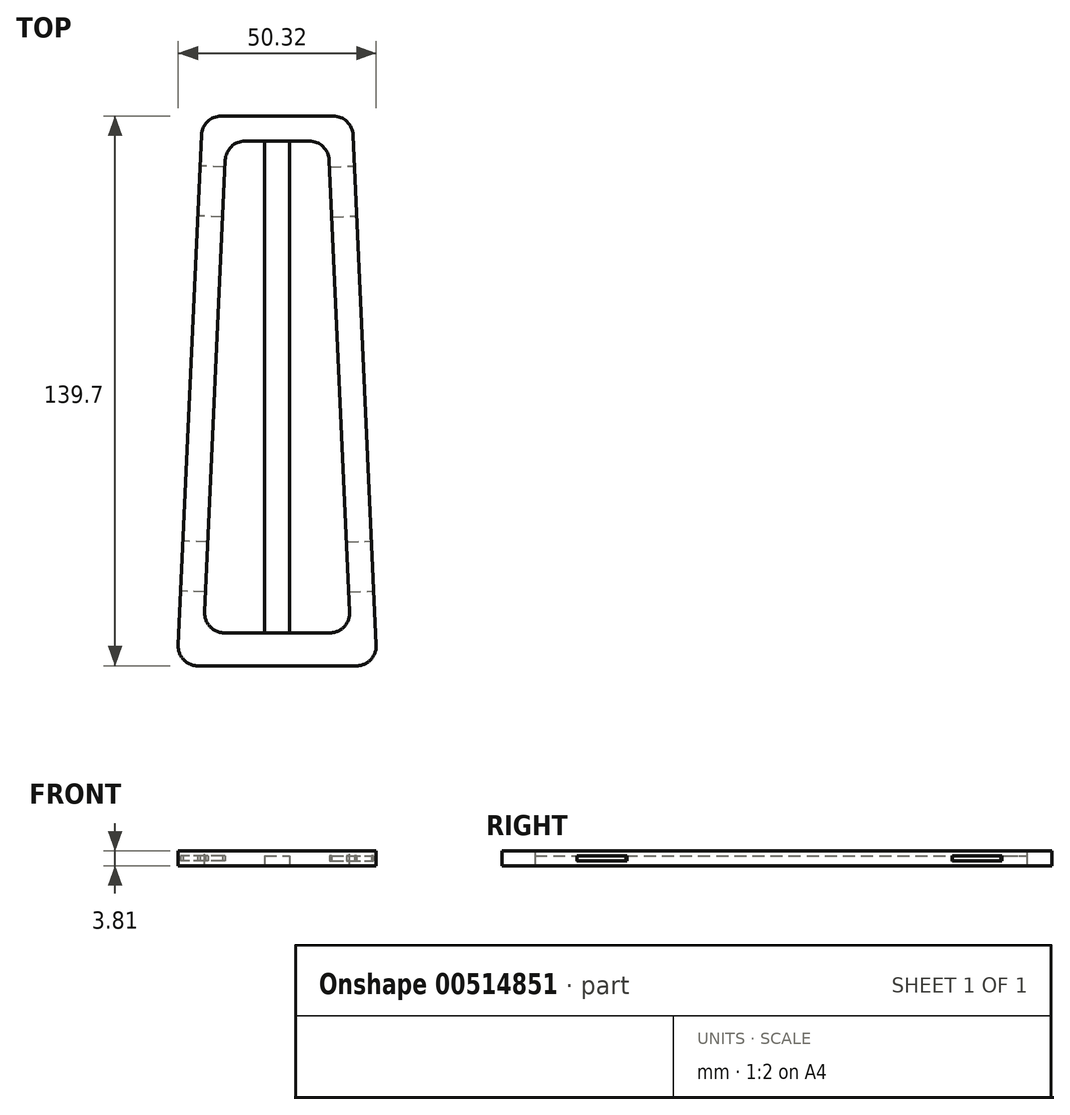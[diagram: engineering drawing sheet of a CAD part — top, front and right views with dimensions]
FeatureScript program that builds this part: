
annotation { "Feature Type Name" : "Feature", "Feature Type Description" : "" }
export const myFeature = defineFeature(function(context is Context, id is Id, definition is map)
    precondition{}
    {
        {
            var Q0;
            Q0=qCreatedBy(makeId("Top.planeOp"),FACE);
            var sketch = newSketch(context, id + "F0", { "sketchPlane" : qUnion([Q0])});
            skLineSegment(sketch, "E0", {"start": v(0, 0) * mm, "end": v(50.8, 0) * mm});
            skLineSegment(sketch, "E1", {"start": v(50.8, 0) * mm, "end": v(44.45, 139.7) * mm});
            skLineSegment(sketch, "E2", {"start": v(44.45, 139.7) * mm, "end": v(6.35, 139.7) * mm});
            skLineSegment(sketch, "E3", {"start": v(6.35, 139.7) * mm, "end": v(0, 0) * mm});
            skLineSegment(sketch, "E4", {"start": v(25.4, 0) * mm, "end": v(25.4, 139.7) * mm, "construction": true});
            skLineSegment(sketch, "E5", {"start": v(6.74, 8.38) * mm, "end": v(44.06, 8.38) * mm, "construction": true});
            skLineSegment(sketch, "E6", {"start": v(44.06, 8.38) * mm, "end": v(38.38, 133.35) * mm});
            skLineSegment(sketch, "E7", {"start": v(38.38, 133.35) * mm, "end": v(12.42, 133.35) * mm, "construction": true});
            skLineSegment(sketch, "E8", {"start": v(12.42, 133.35) * mm, "end": v(6.74, 8.38) * mm});
            skLineSegment(sketch, "E9", {"start": v(22.22, 8.38) * mm, "end": v(22.22, 133.35) * mm});
            skLineSegment(sketch, "E10", {"start": v(28.57, 8.38) * mm, "end": v(28.57, 133.35) * mm});
            skLineSegment(sketch, "E11", {"start": v(6.74, 8.38) * mm, "end": v(22.22, 8.38) * mm});
            skLineSegment(sketch, "E12", {"start": v(28.57, 8.38) * mm, "end": v(44.06, 8.38) * mm});
            skLineSegment(sketch, "E13", {"start": v(28.57, 133.35) * mm, "end": v(38.38, 133.35) * mm});
            skLineSegment(sketch, "E14", {"start": v(22.22, 133.35) * mm, "end": v(12.42, 133.35) * mm});
            skLineSegment(sketch, "E15", {"start": v(22.22, 8.38) * mm, "end": v(28.57, 8.38) * mm});
            skLineSegment(sketch, "E16", {"start": v(22.22, 133.35) * mm, "end": v(28.57, 133.35) * mm});
            skSolve(sketch);
        }
        {
            var Q0;
            Q0=makeQuery(id+"F0.imprint","IMPRINT",FACE,{"disambiguationData":[TD([[makeQuery(id+"F0.imprint","IMPRINT",EDGE,{"derivedFrom":sQuery(id+"F0.wireOp",EDGE,"E0")}),1.0]])]});
            extrude(context, id + "F1", {"entities" : qUnion([Q0]), "depth" : 3.8 * mm, "offsetDistance" : 25.4 * mm});
        }
        {
            var Q0;
            Q0=makeQuery(id+"F0.imprint","IMPRINT",FACE,{"disambiguationData":[TD([[makeQuery(id+"F0.imprint","IMPRINT",EDGE,{"derivedFrom":sQuery(id+"F0.wireOp",EDGE,"E9")}),-1.0]])]});
            extrude(context, id + "F2", {"entities" : qUnion([Q0]), "operationType" : NewBodyOperationType.ADD, "depth" : 2.54 * mm, "offsetDistance" : 25.4 * mm});
        }
        {
            var Q0;
            Q0=makeQuery(id+"F1.opExtrude","SWEPT_FACE",FACE,{"disambiguationData":[OSD([sQuery(id+"F0.wireOp",EDGE,"E3")])]});
            var sketch = newSketch(context, id + "F3", { "sketchPlane" : qUnion([Q0])});
            skLineSegment(sketch, "E17.bottom", {"start": v(-31.75, 2.54) * mm, "end": v(-19.05, 2.54) * mm});
            skLineSegment(sketch, "E17.top", {"start": v(-31.75, 1.27) * mm, "end": v(-19.05, 1.27) * mm});
            skLineSegment(sketch, "E17.left", {"start": v(-31.75, 2.54) * mm, "end": v(-31.75, 1.27) * mm});
            skLineSegment(sketch, "E17.right", {"start": v(-19.05, 2.54) * mm, "end": v(-19.05, 1.27) * mm});
            skPoint(sketch, "E18.firstSnap0", {"position": v(-25.4, 2.54) * mm});
            skPoint(sketch, "E18.oppositeSnap0", {"position": v(-25.4, 1.27) * mm});
            skLineSegment(sketch, "E18.bottom", {"start": v(-127.14, 2.54) * mm, "end": v(-114.44, 2.54) * mm});
            skLineSegment(sketch, "E18.top", {"start": v(-127.14, 1.27) * mm, "end": v(-114.44, 1.27) * mm});
            skLineSegment(sketch, "E18.left", {"start": v(-127.14, 2.54) * mm, "end": v(-127.14, 1.27) * mm});
            skLineSegment(sketch, "E18.right", {"start": v(-114.44, 2.54) * mm, "end": v(-114.44, 1.27) * mm});
            skLineSegment(sketch, "E19", {"start": v(-127.14, 2.54) * mm, "end": v(-127.14, 3.81) * mm, "construction": true});
            skLineSegment(sketch, "E20", {"start": v(-31.75, 2.54) * mm, "end": v(-31.75, 3.81) * mm, "construction": true});
            skLineSegment(sketch, "E21", {"start": v(-31.75, 1.27) * mm, "end": v(-31.75, 0) * mm, "construction": true});
            skLineSegment(sketch, "E22", {"start": v(-127.14, 1.27) * mm, "end": v(-127.14, 0) * mm, "construction": true});
            skSolve(sketch);
        }
        {
            var Q0;
            Q0=makeQuery(id+"F3.imprint","IMPRINT",FACE,{"disambiguationData":[TD([[makeQuery(id+"F3.imprint","IMPRINT",EDGE,{"derivedFrom":sQuery(id+"F3.wireOp",EDGE,"E18.bottom")}),-1.0]])]});
            var Q1;
            Q1=makeQuery(id+"F3.imprint","IMPRINT",FACE,{"disambiguationData":[TD([[makeQuery(id+"F3.imprint","IMPRINT",EDGE,{"derivedFrom":sQuery(id+"F3.wireOp",EDGE,"E17.bottom")}),-1.0]])]});
            extrude(context, id + "F4", {"entities" : qUnion([Q0, Q1]), "operationType" : NewBodyOperationType.REMOVE, "oppositeDirection" : true, "depth" : 6.35 * mm, "offsetDistance" : 25.4 * mm});
        }
        {
            var Q0;
            Q0=makeQuery(id+"F1.opExtrude","SWEPT_FACE",FACE,{"disambiguationData":[OSD([sQuery(id+"F0.wireOp",EDGE,"E1")])]});
            var sketch = newSketch(context, id + "F5", { "sketchPlane" : qUnion([Q0])});
            skLineSegment(sketch, "E23.bottom", {"start": v(16.74, 2.54) * mm, "end": v(29.44, 2.54) * mm});
            skLineSegment(sketch, "E23.top", {"start": v(16.74, 1.27) * mm, "end": v(29.44, 1.27) * mm});
            skLineSegment(sketch, "E23.left", {"start": v(16.74, 2.54) * mm, "end": v(16.74, 1.27) * mm});
            skLineSegment(sketch, "E23.right", {"start": v(29.44, 2.54) * mm, "end": v(29.44, 1.27) * mm});
            skLineSegment(sketch, "E24.bottom", {"start": v(112.14, 2.54) * mm, "end": v(124.84, 2.54) * mm});
            skLineSegment(sketch, "E24.top", {"start": v(112.14, 1.27) * mm, "end": v(124.84, 1.27) * mm});
            skLineSegment(sketch, "E24.left", {"start": v(112.14, 2.54) * mm, "end": v(112.14, 1.27) * mm});
            skLineSegment(sketch, "E24.right", {"start": v(124.84, 2.54) * mm, "end": v(124.84, 1.27) * mm});
            skLineSegment(sketch, "E25", {"start": v(124.84, 1.27) * mm, "end": v(124.84, 0) * mm, "construction": true});
            skLineSegment(sketch, "E26", {"start": v(124.84, 2.54) * mm, "end": v(124.84, 3.81) * mm, "construction": true});
            skLineSegment(sketch, "E27", {"start": v(29.44, 1.27) * mm, "end": v(29.44, 0) * mm, "construction": true});
            skLineSegment(sketch, "E28", {"start": v(29.44, 2.54) * mm, "end": v(29.44, 3.81) * mm, "construction": true});
            skSolve(sketch);
        }
        {
            var Q0;
            Q0 = qSketchRegion(id + "F5", true);
            extrude(context, id + "F6", {"entities" : qUnion([Q0]), "operationType" : NewBodyOperationType.REMOVE, "oppositeDirection" : true, "depth" : 6.35 * mm, "offsetDistance" : 25.4 * mm});
        }
        {
            var Q0;
            Q0=makeQuery(id+"F1.opExtrude","SWEPT_EDGE",EDGE,{"disambiguationData":[OSD([sQuery(id+"F0.wireOp",EDGE,"E0"),sQuery(id+"F0.wireOp",EDGE,"E3")])]});
            var Q1;
            Q1=makeQuery(id+"F1.opExtrude","SWEPT_EDGE",EDGE,{"disambiguationData":[OSD([sQuery(id+"F0.wireOp",EDGE,"E0"),sQuery(id+"F0.wireOp",EDGE,"E1")])]});
            var Q2;
            Q2=makeQuery(id+"F1.opExtrude","SWEPT_EDGE",EDGE,{"disambiguationData":[OSD([sQuery(id+"F0.wireOp",EDGE,"E8"),sQuery(id+"F0.wireOp",EDGE,"E11")])]});
            var Q3;
            Q3=makeQuery(id+"F2.opExtrude","SWEPT_EDGE",EDGE,{"disambiguationData":[OSD([sQuery(id+"F0.wireOp",EDGE,"E9"),sQuery(id+"F0.wireOp",EDGE,"E11"),sQuery(id+"F0.wireOp",EDGE,"E15")])]});
            var Q4;
            Q4=makeQuery(id+"F2.opExtrude","SWEPT_EDGE",EDGE,{"disambiguationData":[OSD([sQuery(id+"F0.wireOp",EDGE,"E10"),sQuery(id+"F0.wireOp",EDGE,"E12"),sQuery(id+"F0.wireOp",EDGE,"E15")])]});
            var Q5;
            Q5=makeQuery(id+"F1.opExtrude","SWEPT_EDGE",EDGE,{"disambiguationData":[OSD([sQuery(id+"F0.wireOp",EDGE,"E6"),sQuery(id+"F0.wireOp",EDGE,"E12")])]});
            var Q6;
            Q6=makeQuery(id+"F1.opExtrude","SWEPT_EDGE",EDGE,{"disambiguationData":[OSD([sQuery(id+"F0.wireOp",EDGE,"E8"),sQuery(id+"F0.wireOp",EDGE,"E14")])]});
            var Q7;
            Q7=makeQuery(id+"F2.opExtrude","SWEPT_EDGE",EDGE,{"disambiguationData":[OSD([sQuery(id+"F0.wireOp",EDGE,"E10"),sQuery(id+"F0.wireOp",EDGE,"E13"),sQuery(id+"F0.wireOp",EDGE,"E16")])]});
            var Q8;
            Q8=makeQuery(id+"F2.opExtrude","SWEPT_EDGE",EDGE,{"disambiguationData":[OSD([sQuery(id+"F0.wireOp",EDGE,"E9"),sQuery(id+"F0.wireOp",EDGE,"E14"),sQuery(id+"F0.wireOp",EDGE,"E16")])]});
            var Q9;
            Q9=makeQuery(id+"F1.opExtrude","SWEPT_EDGE",EDGE,{"disambiguationData":[OSD([sQuery(id+"F0.wireOp",EDGE,"E6"),sQuery(id+"F0.wireOp",EDGE,"E13")])]});
            var Q10;
            Q10=makeQuery(id+"F1.opExtrude","SWEPT_EDGE",EDGE,{"disambiguationData":[OSD([sQuery(id+"F0.wireOp",EDGE,"E2"),sQuery(id+"F0.wireOp",EDGE,"E3")])]});
            var Q11;
            Q11=makeQuery(id+"F1.opExtrude","SWEPT_EDGE",EDGE,{"disambiguationData":[OSD([sQuery(id+"F0.wireOp",EDGE,"E1"),sQuery(id+"F0.wireOp",EDGE,"E2")])]});
            fillet(context, id + "F7", {"entities" : qUnion([Q0, Q1, Q2, Q3, Q4, Q5, Q6, Q7, Q8, Q9, Q10, Q11]), "radius" : 5.08 * mm, "tangentPropagation" : true, "allowEdgeOverflow" : false});
        }
    });
